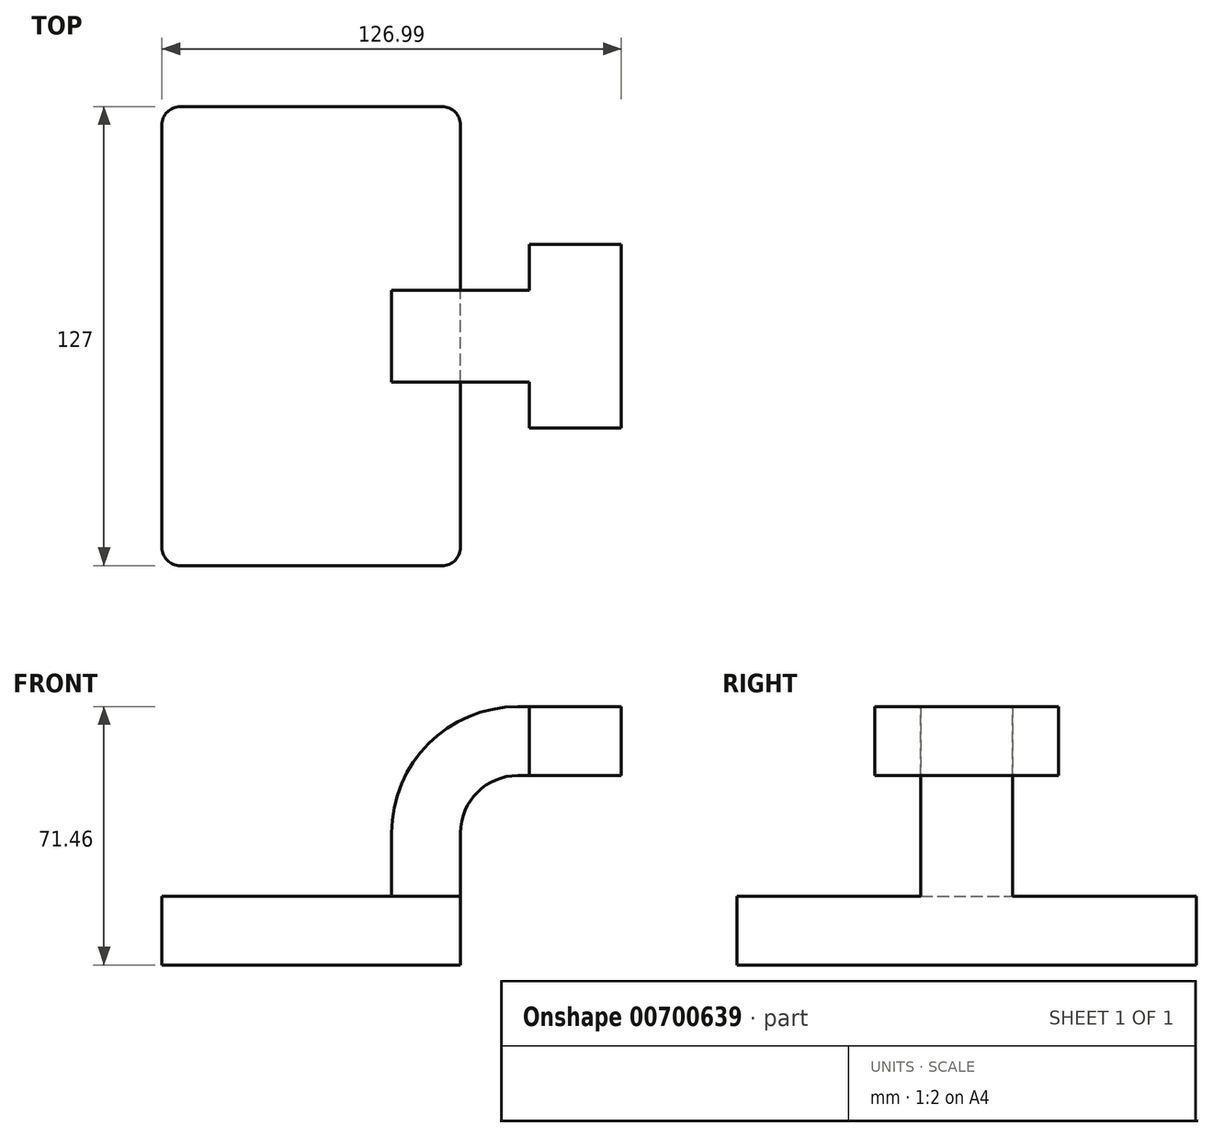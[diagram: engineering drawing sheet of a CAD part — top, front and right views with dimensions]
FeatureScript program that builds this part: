
annotation { "Feature Type Name" : "Feature", "Feature Type Description" : "" }
export const myFeature = defineFeature(function(context is Context, id is Id, definition is map)
    precondition{}
    {
        {
            var Q0;
            Q0=qCreatedBy(makeId("Front.planeOp"),FACE);
            var sketch = newSketch(context, id + "F0", { "sketchPlane" : qUnion([Q0])});
            skLineSegment(sketch, "E0.bottom", {"start": v(41.28, -9.53) * mm, "end": v(-41.28, -9.53) * mm});
            skLineSegment(sketch, "E0.top", {"start": v(41.28, 9.53) * mm, "end": v(-41.28, 9.52) * mm});
            skLineSegment(sketch, "E0.left", {"start": v(41.28, -9.53) * mm, "end": v(41.27, 9.52) * mm});
            skLineSegment(sketch, "E0.right", {"start": v(-41.28, -9.53) * mm, "end": v(-41.28, 9.52) * mm});
            skPoint(sketch, "E0.middle", {"position": v(0, 0) * mm});
            skLineSegment(sketch, "E1.right", {"start": v(41.28, 27) * mm, "end": v(41.28, -1.54) * mm});
            skLineSegment(sketch, "E2.bottom", {"start": v(111.13, 38.1) * mm, "end": v(60.32, 38.1) * mm});
            skLineSegment(sketch, "E2.top", {"start": v(111.12, 66.67) * mm, "end": v(60.32, 66.67) * mm});
            skLineSegment(sketch, "E2.left", {"start": v(111.12, 38.1) * mm, "end": v(111.12, 66.68) * mm});
            skLineSegment(sketch, "E2.right", {"start": v(60.32, 38.1) * mm, "end": v(60.32, 66.68) * mm});
            skArc(sketch, "E3", {"start": v(41.28, 27) * mm, "mid": v(45.92, 38.23) * mm, "end": v(57.15, 42.88) * mm});
            skLineSegment(sketch, "E4", {"start": v(57.15, 42.88) * mm, "end": v(85.72, 42.88) * mm});
            skLineSegment(sketch, "E5.0", {"start": v(57.15, 61.93) * mm, "end": v(85.72, 61.93) * mm});
            skArc(sketch, "E5.1", {"start": v(22.23, 27) * mm, "mid": v(32.45, 51.7) * mm, "end": v(57.15, 61.93) * mm});
            skLineSegment(sketch, "E5.2", {"start": v(22.23, 27) * mm, "end": v(22.23, 9.52) * mm});
            skLineSegment(sketch, "E6", {"start": v(85.72, 66.68) * mm, "end": v(85.72, 38.1) * mm});
            skFitSpline(sketch, "E7", {"points": [v(-41.28, 9.52) * mm, v(57.15, 61.93) * mm], "startDerivative": vector(2.85, 100.05) * mm, "endDerivative": vector(111.73, -10.9) * mm});
            skSolve(sketch);
        }
        {
            var Q0;
            Q0=makeQuery(id+"F0.imprint","IMPRINT",FACE,{"disambiguationData":[TD([[makeQuery(id+"F0.imprint","IMPRINT",EDGE,{"derivedFrom":sQuery(id+"F0.wireOp",EDGE,"E0.bottom")}),-1.0]])]});
            extrude(context, id + "F1", {"entities" : qUnion([Q0]), "endBound" : BoundingType.SYMMETRIC, "depth" : 127 * mm, "offsetDistance" : 25.4 * mm});
        }
        {
            var Q0;
            {var subQ5=sQuery(id+"F0.wireOp",EDGE,"E3");Q0=makeQuery(id+"F0.imprint","IMPRINT",FACE,{"disambiguationData":[TD([[makeQuery(id+"F0.imprint","IMPRINT",EDGE,{"derivedFrom":subQ5}),1.0]])]});}
            var Q1;
            {var subQ0=sQuery(id+"F0.wireOp",EDGE,"E4");var subQ1=sQuery(id+"F0.wireOp",EDGE,"E2.right");var subQ2=makeQuery(id+"F0.imprint","INTERSECT",VERTEX,{"derivedFrom":[subQ1,subQ0]});Q1=makeQuery(id+"F0.imprint","IMPRINT",FACE,{"disambiguationData":[TD([[makeQuery(id+"F0.imprint","IMPRINT",EDGE,{"disambiguationData":[TD([[subQ2,-1.0]])],"derivedFrom":subQ1}),-1.0]])]});}
            extrude(context, id + "F2", {"entities" : qUnion([Q0, Q1]), "operationType" : NewBodyOperationType.ADD, "endBound" : BoundingType.SYMMETRIC, "depth" : 50.8 * mm, "offsetDistance" : 25.4 * mm});
        }
        {
            var Q0;
            Q0=makeQuery(id+"F1.opExtrude","CAP_EDGE",EDGE,{"disambiguationData":[OSD([sQuery(id+"F0.wireOp",EDGE,"E0.right")])],"isStart":false});
            fillet(context, id + "F3", {"entities" : qUnion([Q0]), "radius" : 5.08 * mm, "tangentPropagation" : true, "allowEdgeOverflow" : false});
        }
        {
            var Q0;
            Q0=makeQuery(id+"F1.opExtrude","CAP_EDGE",EDGE,{"disambiguationData":[OSD([sQuery(id+"F0.wireOp",EDGE,"E0.right")])],"isStart":true});
            var Q1;
            Q1=makeQuery(id+"F1.opExtrude","CAP_EDGE",EDGE,{"disambiguationData":[OSD([sQuery(id+"F0.wireOp",EDGE,"E0.left"),sQuery(id+"F0.wireOp",EDGE,"E1.right")])],"isStart":true});
            fillet(context, id + "F4", {"entities" : qUnion([Q0, Q1]), "radius" : 5.08 * mm, "tangentPropagation" : true, "allowEdgeOverflow" : false});
        }
        {
            var Q0;
            Q0=makeQuery(id+"F1.opExtrude","CAP_EDGE",EDGE,{"disambiguationData":[OSD([sQuery(id+"F0.wireOp",EDGE,"E0.left"),sQuery(id+"F0.wireOp",EDGE,"E1.right")])],"isStart":false});
            fillet(context, id + "F5", {"entities" : qUnion([Q0]), "radius" : 5.08 * mm, "tangentPropagation" : true, "allowEdgeOverflow" : false});
        }
        {
            var Q0;
            Q0=makeQuery(id+"F0.imprint","IMPRINT",FACE,{"disambiguationData":[TD([[makeQuery(id+"F0.imprint","IMPRINT",EDGE,{"derivedFrom":sQuery(id+"F0.wireOp",EDGE,"E5.1")}),1.0]])]});
            extrude(context, id + "F6", {"entities" : qUnion([Q0]), "operationType" : NewBodyOperationType.ADD, "endBound" : BoundingType.SYMMETRIC, "depth" : 25.4 * mm, "offsetDistance" : 25.4 * mm});
        }
    });
